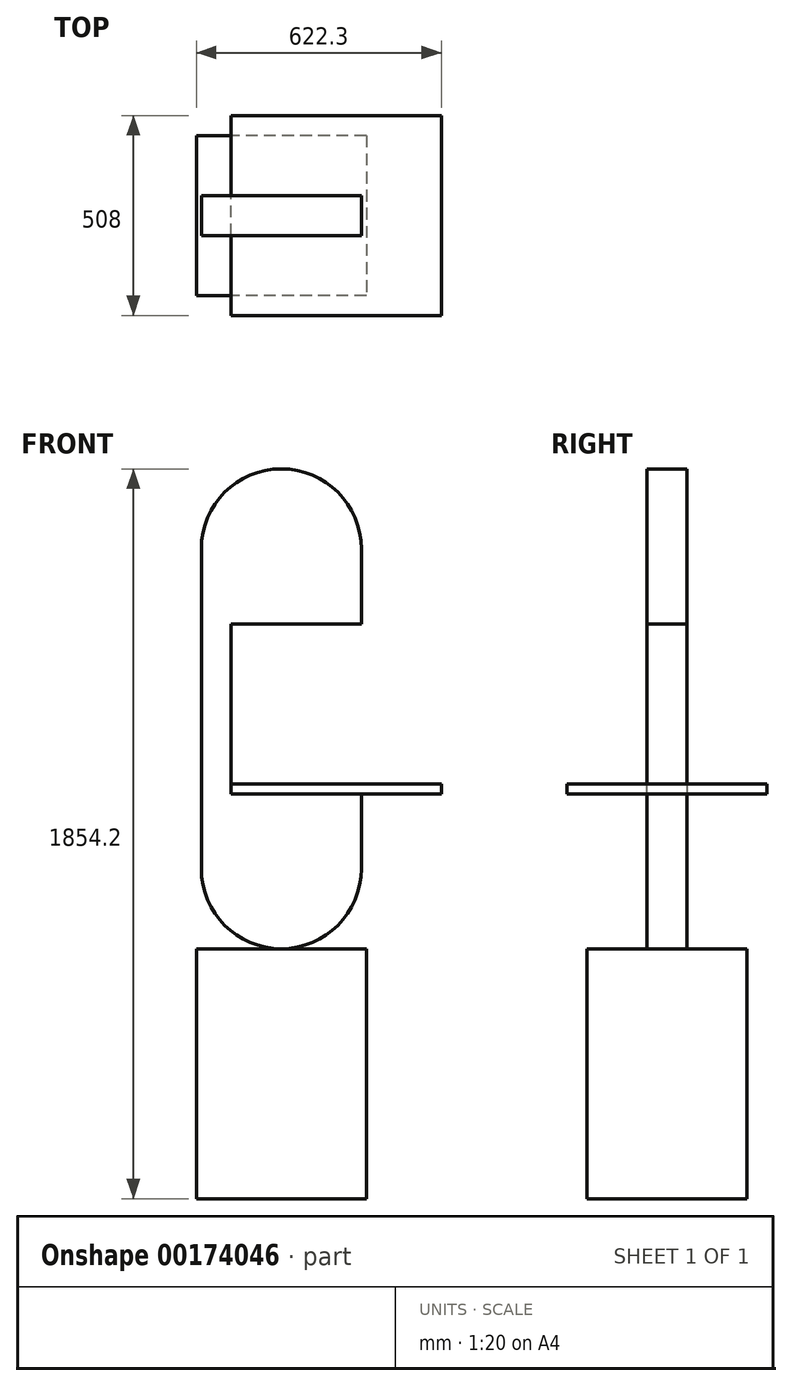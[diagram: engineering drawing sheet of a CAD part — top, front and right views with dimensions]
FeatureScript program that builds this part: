
annotation { "Feature Type Name" : "Feature", "Feature Type Description" : "" }
export const myFeature = defineFeature(function(context is Context, id is Id, definition is map)
    precondition{}
    {
        {
            var Q0;
            Q0=qCreatedBy(makeId("Top.planeOp"),FACE);
            var sketch = newSketch(context, id + "F0", { "sketchPlane" : qUnion([Q0])});
            skLineSegment(sketch, "E0.bottom", {"start": v(215.9, 203.2) * mm, "end": v(-215.9, 203.2) * mm});
            skLineSegment(sketch, "E0.top", {"start": v(215.9, -203.2) * mm, "end": v(-215.9, -203.2) * mm});
            skLineSegment(sketch, "E0.left", {"start": v(215.9, 203.2) * mm, "end": v(215.9, -203.2) * mm});
            skLineSegment(sketch, "E0.right", {"start": v(-215.9, 203.2) * mm, "end": v(-215.9, -203.2) * mm});
            skPoint(sketch, "E0.middle", {"position": v(0, 0) * mm});
            skSolve(sketch);
        }
        {
            var Q0;
            Q0=makeQuery(id+"F0.imprint","IMPRINT",FACE,{"disambiguationData":[TD([[makeQuery(id+"F0.imprint","IMPRINT",EDGE,{"derivedFrom":sQuery(id+"F0.wireOp",EDGE,"E0.bottom")}),1.0]])]});
            extrude(context, id + "F1", {"entities" : qUnion([Q0]), "depth" : 635 * mm});
        }
        {
            var Q0;
            Q0=qCreatedBy(makeId("Front.planeOp"),FACE);
            var sketch = newSketch(context, id + "F2", { "sketchPlane" : qUnion([Q0])});
            skCircle(sketch, "E1", {"center": v(0, 838.2) * mm, "radius": 177.8 * mm});
            skCircle(sketch, "E2", {"center": v(0, 1651) * mm, "radius": 177.8 * mm});
            skLineSegment(sketch, "E3", {"start": v(-203.2, 1651) * mm, "end": v(-203.2, 838.2) * mm});
            skArc(sketch, "E4", {"start": v(-203.2, 838.2) * mm, "mid": v(0, 635) * mm, "end": v(203.2, 838.2) * mm});
            skLineSegment(sketch, "E5", {"start": v(203.2, 838.2) * mm, "end": v(203.2, 1028.7) * mm});
            skArc(sketch, "E6", {"start": v(203.2, 1651) * mm, "mid": v(0, 1854.2) * mm, "end": v(-203.2, 1651) * mm});
            skLineSegment(sketch, "E7", {"start": v(203.2, 1651) * mm, "end": v(203.2, 1460.5) * mm});
            skLineSegment(sketch, "E8", {"start": v(203.2, 1460.5) * mm, "end": v(-203.2, 1460.5) * mm});
            skLineSegment(sketch, "E9", {"start": v(203.2, 1028.7) * mm, "end": v(-203.2, 1028.7) * mm});
            skLineSegment(sketch, "E10", {"start": v(-127, 1460.5) * mm, "end": v(-127, 1028.7) * mm});
            skLineSegment(sketch, "E11", {"start": v(-127, 1054.1) * mm, "end": v(406.4, 1054.1) * mm});
            skLineSegment(sketch, "E12", {"start": v(203.2, 1028.7) * mm, "end": v(406.4, 1028.7) * mm});
            skLineSegment(sketch, "E13", {"start": v(406.4, 1028.7) * mm, "end": v(406.4, 1054.1) * mm});
            skSolve(sketch);
        }
        {
            var Q0;
            Q0=makeQuery(id+"F2.imprint","IMPRINT",FACE,{"disambiguationData":[TD([[makeQuery(id+"F2.imprint","IMPRINT",EDGE,{"derivedFrom":sQuery(id+"F2.wireOp",EDGE,"E1")}),-1.0]])]});
            var Q1;
            Q1=makeQuery(id+"F2.imprint","IMPRINT",FACE,{"disambiguationData":[TD([[makeQuery(id+"F2.imprint","IMPRINT",EDGE,{"derivedFrom":sQuery(id+"F2.wireOp",EDGE,"E2")}),-1.0]])]});
            var Q2;
            {var subQ1=sQuery(id+"F2.wireOp",EDGE,"E8");var subQ5=sQuery(id+"F2.wireOp",EDGE,"E3");var subQ8=makeQuery(id+"F2.imprint","INTERSECT",VERTEX,{"derivedFrom":[subQ5,subQ1]});Q2=makeQuery(id+"F2.imprint","IMPRINT",FACE,{"disambiguationData":[TD([[makeQuery(id+"F2.imprint","IMPRINT",EDGE,{"disambiguationData":[TD([[subQ8,-1.0]])],"derivedFrom":subQ5}),1.0]])]});}
            var Q3;
            Q3=makeQuery(id+"F2.imprint","IMPRINT",FACE,{"disambiguationData":[TD([[makeQuery(id+"F2.imprint","IMPRINT",EDGE,{"derivedFrom":sQuery(id+"F2.wireOp",EDGE,"E2")}),1.0]])]});
            var Q4;
            Q4=makeQuery(id+"F2.imprint","IMPRINT",FACE,{"disambiguationData":[TD([[makeQuery(id+"F2.imprint","IMPRINT",EDGE,{"derivedFrom":sQuery(id+"F2.wireOp",EDGE,"E1")}),1.0]])]});
            extrude(context, id + "F3", {"entities" : qUnion([Q0, Q1, Q2, Q3, Q4]), "depth" : 101.6 * mm, "symmetric" : true});
        }
        {
            var Q0;
            {var subQ4=sQuery(id+"F2.wireOp",EDGE,"E11");Q0=makeQuery(id+"F2.imprint","IMPRINT",FACE,{"disambiguationData":[TD([[makeQuery(id+"F2.imprint","IMPRINT",EDGE,{"derivedFrom":subQ4}),-1.0]])]});}
            extrude(context, id + "F4", {"entities" : qUnion([Q0]), "operationType" : NewBodyOperationType.ADD, "depth" : 508 * mm, "symmetric" : true});
        }
    });
